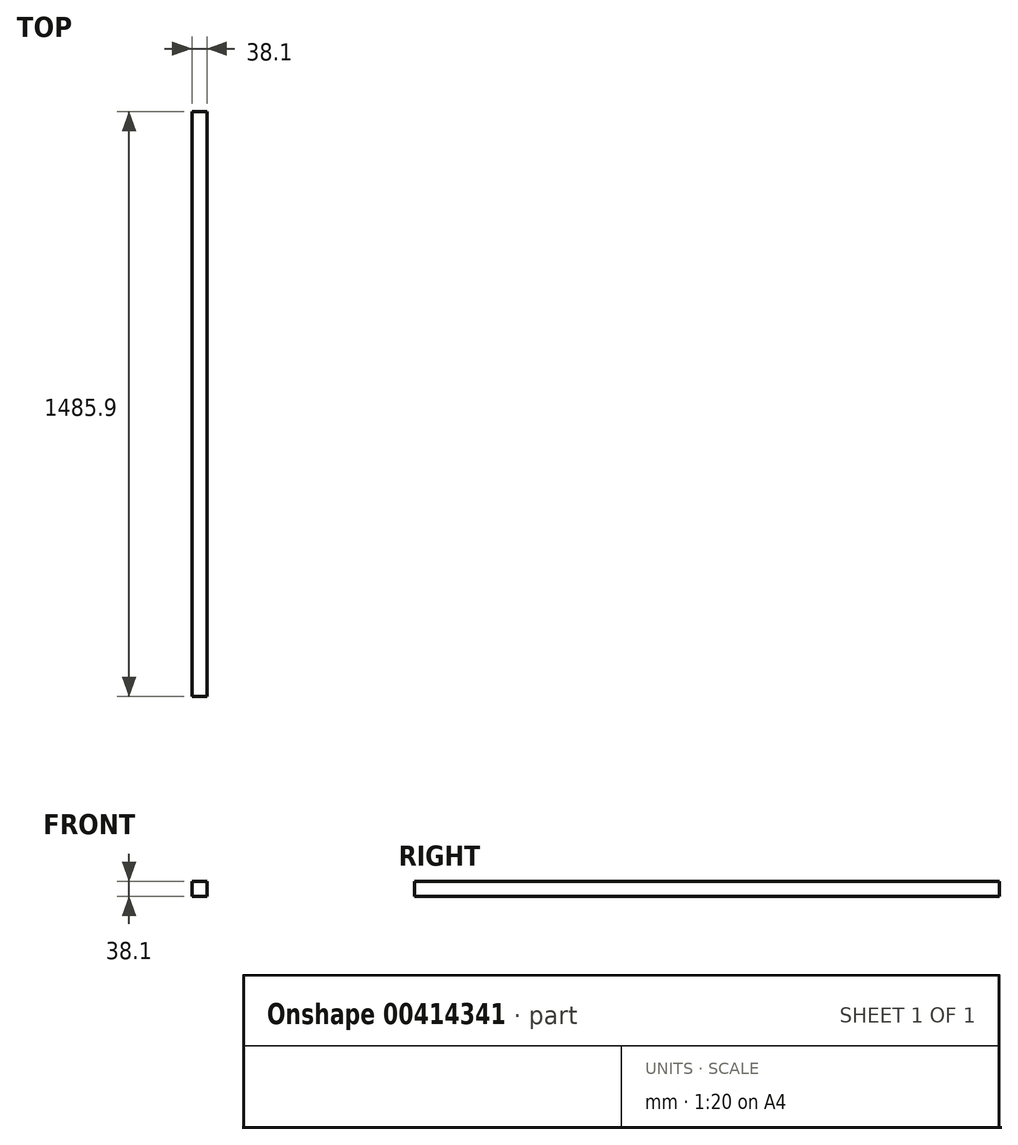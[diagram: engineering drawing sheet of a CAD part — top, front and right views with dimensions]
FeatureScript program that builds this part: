
annotation { "Feature Type Name" : "Feature", "Feature Type Description" : "" }
export const myFeature = defineFeature(function(context is Context, id is Id, definition is map)
    precondition{}
    {
        {
            var Q0;
            Q0=qCreatedBy(makeId("Top.planeOp"),FACE);
            var sketch = newSketch(context, id + "F0", { "sketchPlane" : qUnion([Q0])});
            skLineSegment(sketch, "E0.bottom", {"start": v(-19.05, 742.95) * mm, "end": v(19.05, 742.95) * mm});
            skLineSegment(sketch, "E0.top", {"start": v(-19.05, -742.95) * mm, "end": v(19.05, -742.95) * mm});
            skLineSegment(sketch, "E0.left", {"start": v(-19.05, 742.95) * mm, "end": v(-19.05, -742.95) * mm});
            skLineSegment(sketch, "E0.right", {"start": v(19.05, 742.95) * mm, "end": v(19.05, -742.95) * mm});
            skPoint(sketch, "E0.middle", {"position": v(0, 0) * mm});
            skSolve(sketch);
        }
        {
            var Q0;
            Q0 = qSketchRegion(id + "F0", true);
            extrude(context, id + "F1", {"entities" : qUnion([Q0]), "depth" : 38.1 * mm});
        }
    });
